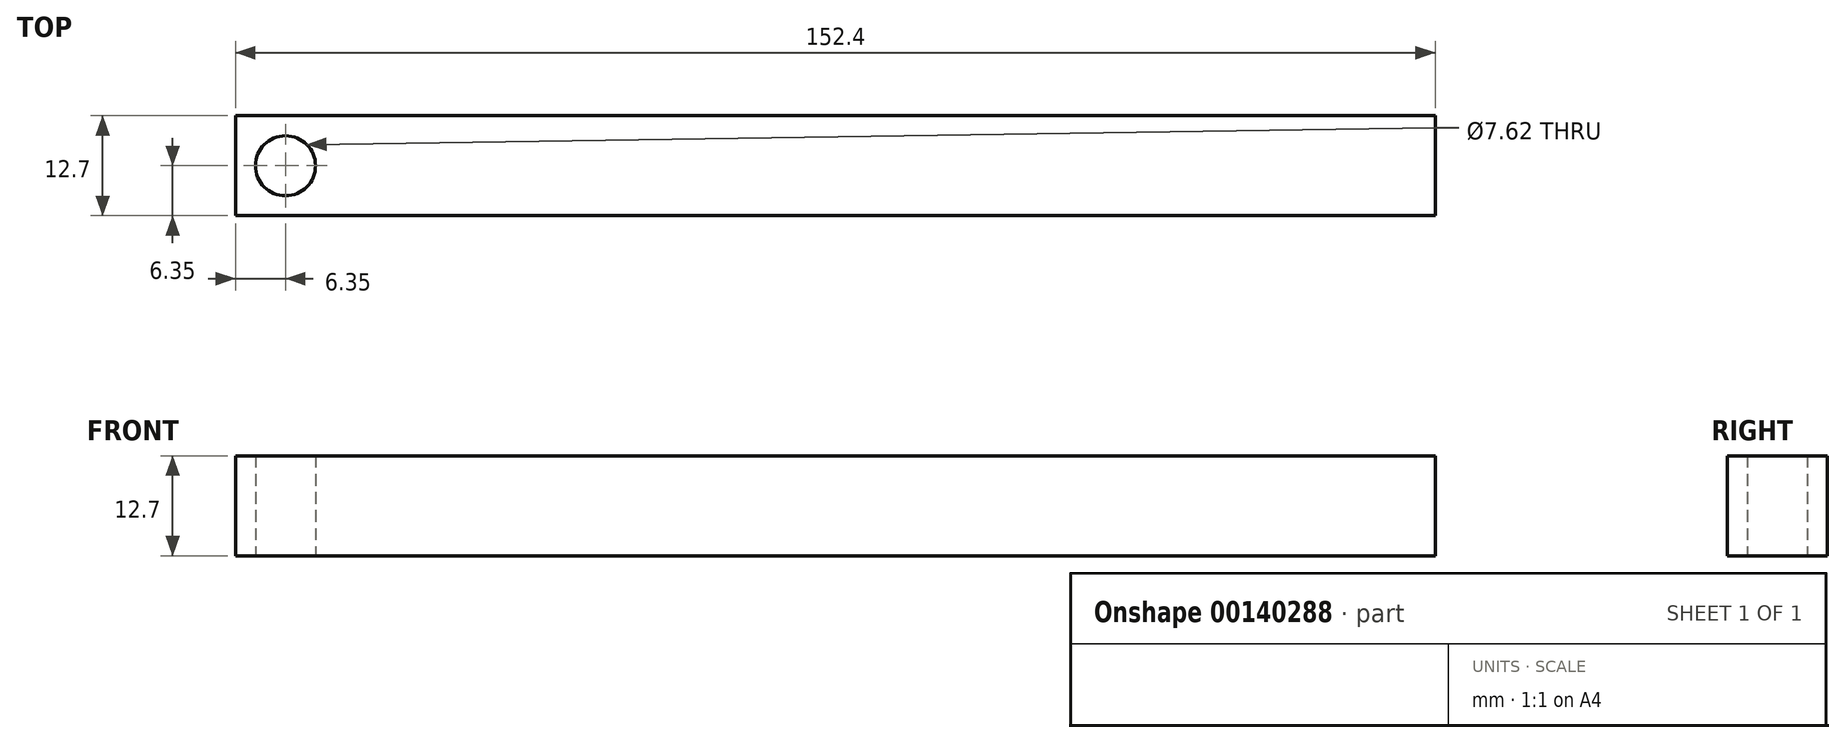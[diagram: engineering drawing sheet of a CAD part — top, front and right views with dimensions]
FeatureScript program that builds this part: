
annotation { "Feature Type Name" : "Feature", "Feature Type Description" : "" }
export const myFeature = defineFeature(function(context is Context, id is Id, definition is map)
    precondition{}
    {
        {
            var Q0;
            Q0=qCreatedBy(makeId("Top.planeOp"),FACE);
            var sketch = newSketch(context, id + "F0", { "sketchPlane" : qUnion([Q0])});
            skLineSegment(sketch, "E0.bottom", {"start": v(-152.4, 0) * mm, "end": v(0, 0) * mm});
            skLineSegment(sketch, "E0.top", {"start": v(-152.4, -12.7) * mm, "end": v(0, -12.7) * mm});
            skLineSegment(sketch, "E0.left", {"start": v(-152.4, 0) * mm, "end": v(-152.4, -12.7) * mm});
            skLineSegment(sketch, "E0.right", {"start": v(0, 0) * mm, "end": v(0, -12.7) * mm});
            skLineSegment(sketch, "E1.bottom", {"start": v(-152.4, -12.7) * mm, "end": v(-139.7, -12.7) * mm});
            skLineSegment(sketch, "E1.top", {"start": v(-152.4, 0) * mm, "end": v(-139.7, 0) * mm});
            skLineSegment(sketch, "E1.left", {"start": v(-152.4, -12.7) * mm, "end": v(-152.4, 0) * mm});
            skCircle(sketch, "E2", {"center": v(-146.05, -6.35) * mm, "radius": 3.81 * mm});
            skSolve(sketch);
        }
        {
            var Q0;
            Q0=makeQuery(id+"F0.imprint","IMPRINT",FACE,{"disambiguationData":[TD([[makeQuery(id+"F0.imprint","IMPRINT",EDGE,{"derivedFrom":sQuery(id+"F0.wireOp",EDGE,"E0.bottom")}),-1.0]])]});
            extrude(context, id + "F1", {"entities" : qUnion([Q0]), "depth" : 12.7 * mm});
        }
    });
